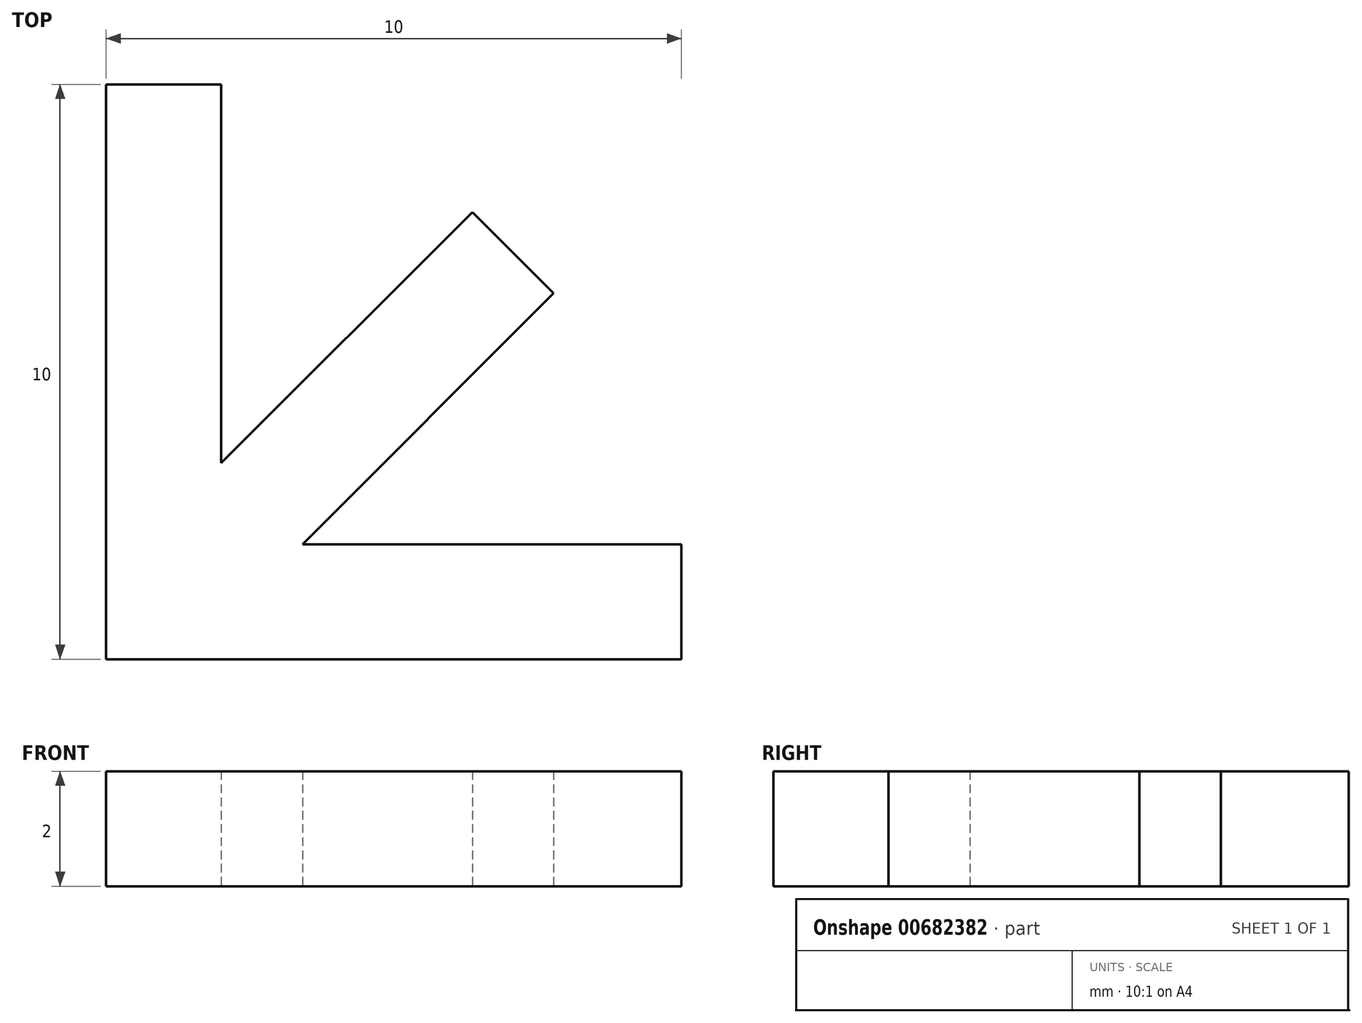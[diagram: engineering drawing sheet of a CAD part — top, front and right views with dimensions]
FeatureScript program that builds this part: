
annotation { "Feature Type Name" : "Feature", "Feature Type Description" : "" }
export const myFeature = defineFeature(function(context is Context, id is Id, definition is map)
    precondition{}
    {
        {
            var Q0;
            Q0=qCreatedBy(makeId("Top.planeOp"),FACE);
            var sketch = newSketch(context, id + "F0", { "sketchPlane" : qUnion([Q0])});
            skLineSegment(sketch, "E0.right", {"start": v(10, 2) * mm, "end": v(10, 0) * mm});
            skLineSegment(sketch, "E1.top", {"start": v(0, 10) * mm, "end": v(2, 10) * mm});
            skLineSegment(sketch, "E1.left", {"start": v(0, 0) * mm, "end": v(0, 10) * mm});
            skLineSegment(sketch, "E1.right", {"start": v(2, 3.41) * mm, "end": v(2, 10) * mm});
            skLineSegment(sketch, "E2", {"start": v(6.36, 7.78) * mm, "end": v(7.78, 6.36) * mm});
            skLineSegment(sketch, "E3", {"start": v(7.78, 6.36) * mm, "end": v(3.41, 2) * mm});
            skLineSegment(sketch, "E4", {"start": v(7.07, 7.07) * mm, "end": v(0, 0) * mm, "construction": true});
            skLineSegment(sketch, "E5.trimOffspring", {"start": v(2, 3.41) * mm, "end": v(6.36, 7.78) * mm});
            skLineSegment(sketch, "E6.trimOffspring", {"start": v(3.41, 2) * mm, "end": v(10, 2) * mm});
            skLineSegment(sketch, "E7", {"start": v(0, 0) * mm, "end": v(10, 0) * mm});
            skSolve(sketch);
        }
        {
            var Q0;
            Q0=qSketchRegion(id+"F0",true);
            extrude(context, id + "F1", {"entities" : qUnion([Q0]), "depth" : 2 * mm, "offsetDistance" : 25 * mm});
        }
    });
